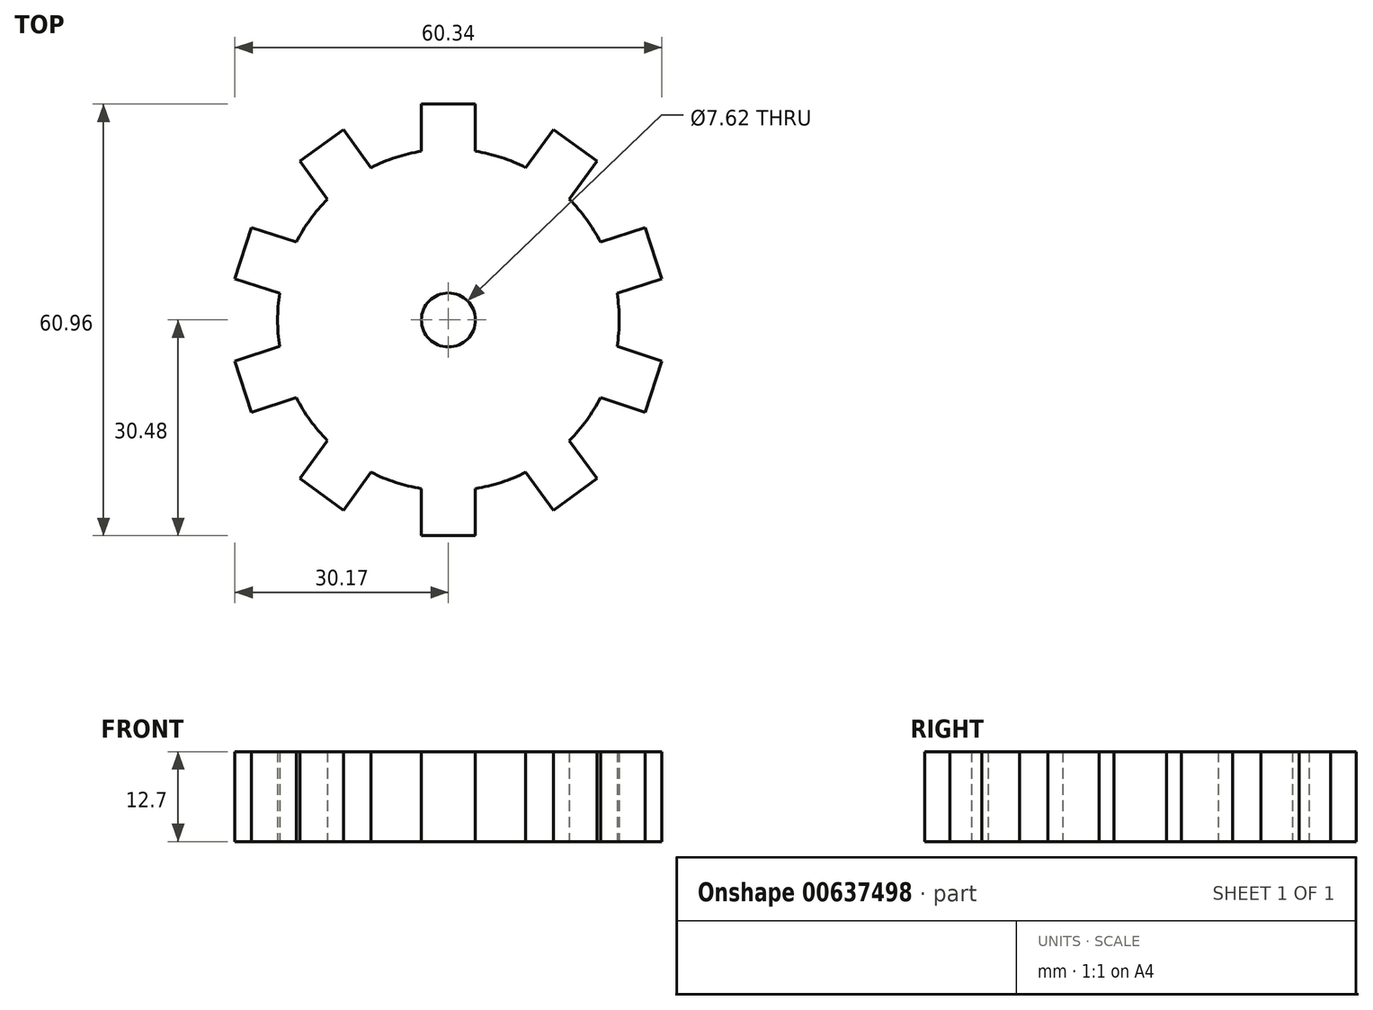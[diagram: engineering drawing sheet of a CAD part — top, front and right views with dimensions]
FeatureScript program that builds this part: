
annotation { "Feature Type Name" : "Feature", "Feature Type Description" : "" }
export const myFeature = defineFeature(function(context is Context, id is Id, definition is map)
    precondition{}
    {
        {
            var Q0;
            Q0=qCreatedBy(makeId("Top.planeOp"),FACE);
            var sketch = newSketch(context, id + "F0", { "sketchPlane" : qUnion([Q0])});
            skCircle(sketch, "E0", {"center": v(0, 0) * mm, "radius": 24.13 * mm});
            skLineSegment(sketch, "E1", {"start": v(0, 0) * mm, "end": v(-3.81, 0) * mm});
            skLineSegment(sketch, "E2", {"start": v(-3.81, 0) * mm, "end": v(-3.81, 30.48) * mm});
            skLineSegment(sketch, "E3", {"start": v(-3.81, 30.48) * mm, "end": v(3.8, 30.48) * mm});
            skLineSegment(sketch, "E4", {"start": v(3.81, 30.48) * mm, "end": v(3.81, 0) * mm});
            skLineSegment(sketch, "E5", {"start": v(3.81, 0) * mm, "end": v(0, 0) * mm});
            skLineSegment(sketch, "E6.1.0", {"start": v(-3.08, -2.24) * mm, "end": v(-21, 22.42) * mm});
            skLineSegment(sketch, "E6.1.1", {"start": v(-14.83, 26.9) * mm, "end": v(3.08, 2.24) * mm});
            skLineSegment(sketch, "E6.1.2", {"start": v(-21, 22.42) * mm, "end": v(-14.83, 26.9) * mm});
            skLineSegment(sketch, "E6.2.0", {"start": v(-1.18, -3.62) * mm, "end": v(-30.17, 5.8) * mm});
            skLineSegment(sketch, "E6.2.1", {"start": v(-27.81, 13.04) * mm, "end": v(1.18, 3.62) * mm});
            skLineSegment(sketch, "E6.2.2", {"start": v(-30.17, 5.8) * mm, "end": v(-27.81, 13.04) * mm});
            skLineSegment(sketch, "E6.3.0", {"start": v(1.18, -3.62) * mm, "end": v(-27.81, -13.04) * mm});
            skLineSegment(sketch, "E6.3.1", {"start": v(-30.17, -5.8) * mm, "end": v(-1.18, 3.62) * mm});
            skLineSegment(sketch, "E6.3.2", {"start": v(-27.81, -13.04) * mm, "end": v(-30.17, -5.8) * mm});
            skLineSegment(sketch, "E6.4.0", {"start": v(3.08, -2.24) * mm, "end": v(-14.83, -26.9) * mm});
            skLineSegment(sketch, "E6.4.1", {"start": v(-21, -22.42) * mm, "end": v(-3.08, 2.24) * mm});
            skLineSegment(sketch, "E6.4.2", {"start": v(-14.83, -26.9) * mm, "end": v(-21, -22.42) * mm});
            skLineSegment(sketch, "E6.5.0", {"start": v(3.81, 0) * mm, "end": v(3.81, -30.48) * mm});
            skLineSegment(sketch, "E6.5.1", {"start": v(-3.8, -30.48) * mm, "end": v(-3.8, 0) * mm});
            skLineSegment(sketch, "E6.5.2", {"start": v(3.81, -30.48) * mm, "end": v(-3.81, -30.48) * mm});
            skLineSegment(sketch, "E6.6.0", {"start": v(3.08, 2.24) * mm, "end": v(21, -22.42) * mm});
            skLineSegment(sketch, "E6.6.1", {"start": v(14.83, -26.9) * mm, "end": v(-3.08, -2.24) * mm});
            skLineSegment(sketch, "E6.6.2", {"start": v(21, -22.42) * mm, "end": v(14.83, -26.9) * mm});
            skLineSegment(sketch, "E6.7.0", {"start": v(1.18, 3.62) * mm, "end": v(30.17, -5.8) * mm});
            skLineSegment(sketch, "E6.7.1", {"start": v(27.81, -13.04) * mm, "end": v(-1.18, -3.62) * mm});
            skLineSegment(sketch, "E6.7.2", {"start": v(30.17, -5.8) * mm, "end": v(27.81, -13.04) * mm});
            skLineSegment(sketch, "E6.8.0", {"start": v(-1.18, 3.62) * mm, "end": v(27.81, 13.04) * mm});
            skLineSegment(sketch, "E6.8.1", {"start": v(30.17, 5.8) * mm, "end": v(1.18, -3.62) * mm});
            skLineSegment(sketch, "E6.8.2", {"start": v(27.81, 13.04) * mm, "end": v(30.17, 5.8) * mm});
            skLineSegment(sketch, "E6.9.0", {"start": v(-3.08, 2.24) * mm, "end": v(14.83, 26.9) * mm});
            skLineSegment(sketch, "E6.9.1", {"start": v(21, 22.42) * mm, "end": v(3.08, -2.24) * mm});
            skLineSegment(sketch, "E6.9.2", {"start": v(14.83, 26.9) * mm, "end": v(21, 22.42) * mm});
            skSolve(sketch);
        }
        {
            var Q0;
            Q0 = qSketchRegion(id + "F0", true);
            var Q1;
            {var subQ0=sQuery(id+"F0.wireOp",EDGE,"E6.12.1");var subQ1=sQuery(id+"F0.wireOp",EDGE,"E6.9.0");var subQ2=makeQuery(id+"F0.imprint","INTERSECT",VERTEX,{"derivedFrom":[subQ1,subQ0]});Q1=makeQuery(id+"F0.imprint","IMPRINT",FACE,{"disambiguationData":[TD([[makeQuery(id+"F0.imprint","IMPRINT",EDGE,{"disambiguationData":[TD([[subQ2,-1.0]])],"derivedFrom":subQ1}),1.0]])]});}
            var Q2;
            {var subQ0=sQuery(id+"F0.wireOp",EDGE,"E6.13.1");var subQ1=sQuery(id+"F0.wireOp",EDGE,"E6.10.0");var subQ2=makeQuery(id+"F0.imprint","INTERSECT",VERTEX,{"derivedFrom":[subQ1,subQ0]});Q2=makeQuery(id+"F0.imprint","IMPRINT",FACE,{"disambiguationData":[TD([[makeQuery(id+"F0.imprint","IMPRINT",EDGE,{"disambiguationData":[TD([[subQ2,-1.0]])],"derivedFrom":subQ1}),1.0]])]});}
            var Q3;
            {var subQ0=sQuery(id+"F0.wireOp",EDGE,"E6.13.1");var subQ1=sQuery(id+"F0.wireOp",EDGE,"E6.9.0");var subQ2=makeQuery(id+"F0.imprint","INTERSECT",VERTEX,{"derivedFrom":[subQ1,subQ0]});Q3=makeQuery(id+"F0.imprint","IMPRINT",FACE,{"disambiguationData":[TD([[makeQuery(id+"F0.imprint","IMPRINT",EDGE,{"disambiguationData":[TD([[subQ2,-1.0]])],"derivedFrom":subQ1}),1.0]])]});}
            var Q4;
            {var subQ0=sQuery(id+"F0.wireOp",EDGE,"E6.10.0");var subQ1=sQuery(id+"F0.wireOp",EDGE,"E4");var subQ2=makeQuery(id+"F0.imprint","INTERSECT",VERTEX,{"derivedFrom":[subQ1,subQ0]});Q4=makeQuery(id+"F0.imprint","IMPRINT",FACE,{"disambiguationData":[TD([[makeQuery(id+"F0.imprint","IMPRINT",EDGE,{"disambiguationData":[TD([[subQ2,-1.0]])],"derivedFrom":subQ1}),1.0]])]});}
            var Q5;
            {var subQ0=sQuery(id+"F0.wireOp",EDGE,"E6.11.0");var subQ1=sQuery(id+"F0.wireOp",EDGE,"E4");var subQ2=makeQuery(id+"F0.imprint","INTERSECT",VERTEX,{"derivedFrom":[subQ1,subQ0]});Q5=makeQuery(id+"F0.imprint","IMPRINT",FACE,{"disambiguationData":[TD([[makeQuery(id+"F0.imprint","IMPRINT",EDGE,{"disambiguationData":[TD([[subQ2,-1.0]])],"derivedFrom":subQ1}),1.0]])]});}
            var Q6;
            {var subQ0=sQuery(id+"F0.wireOp",EDGE,"E6.12.0");var subQ1=sQuery(id+"F0.wireOp",EDGE,"E4");var subQ2=makeQuery(id+"F0.imprint","INTERSECT",VERTEX,{"derivedFrom":[subQ1,subQ0]});Q6=makeQuery(id+"F0.imprint","IMPRINT",FACE,{"disambiguationData":[TD([[makeQuery(id+"F0.imprint","IMPRINT",EDGE,{"disambiguationData":[TD([[subQ2,-1.0]])],"derivedFrom":subQ1}),1.0]])]});}
            var Q7;
            {var subQ0=sQuery(id+"F0.wireOp",EDGE,"E6.12.0");var subQ1=sQuery(id+"F0.wireOp",EDGE,"E4");var subQ2=makeQuery(id+"F0.imprint","INTERSECT",VERTEX,{"derivedFrom":[subQ1,subQ0]});Q7=makeQuery(id+"F0.imprint","IMPRINT",FACE,{"disambiguationData":[TD([[makeQuery(id+"F0.imprint","IMPRINT",EDGE,{"disambiguationData":[TD([[subQ2,-1.0]])],"derivedFrom":subQ1}),-1.0]])]});}
            var Q8;
            {var subQ0=sQuery(id+"F0.wireOp",EDGE,"E6.11.0");var subQ1=sQuery(id+"F0.wireOp",EDGE,"E4");var subQ2=makeQuery(id+"F0.imprint","INTERSECT",VERTEX,{"derivedFrom":[subQ1,subQ0]});Q8=makeQuery(id+"F0.imprint","IMPRINT",FACE,{"disambiguationData":[TD([[makeQuery(id+"F0.imprint","IMPRINT",EDGE,{"disambiguationData":[TD([[subQ2,-1.0]])],"derivedFrom":subQ1}),-1.0]])]});}
            var Q9;
            {var subQ0=sQuery(id+"F0.wireOp",EDGE,"E6.13.0");var subQ1=sQuery(id+"F0.wireOp",EDGE,"E4");var subQ2=makeQuery(id+"F0.imprint","INTERSECT",VERTEX,{"derivedFrom":[subQ1,subQ0]});Q9=makeQuery(id+"F0.imprint","IMPRINT",FACE,{"disambiguationData":[TD([[makeQuery(id+"F0.imprint","IMPRINT",EDGE,{"disambiguationData":[TD([[subQ2,-1.0]])],"derivedFrom":subQ1}),-1.0]])]});}
            var Q10;
            {var subQ0=sQuery(id+"F0.wireOp",EDGE,"E6.13.0");var subQ1=sQuery(id+"F0.wireOp",EDGE,"E6.1.1");var subQ2=makeQuery(id+"F0.imprint","INTERSECT",VERTEX,{"derivedFrom":[subQ1,subQ0]});Q10=makeQuery(id+"F0.imprint","IMPRINT",FACE,{"disambiguationData":[TD([[makeQuery(id+"F0.imprint","IMPRINT",EDGE,{"disambiguationData":[TD([[subQ2,-1.0]])],"derivedFrom":subQ1}),-1.0]])]});}
            var Q11;
            {var subQ0=sQuery(id+"F0.wireOp",EDGE,"E6.12.0");var subQ1=sQuery(id+"F0.wireOp",EDGE,"E6.1.1");var subQ2=makeQuery(id+"F0.imprint","INTERSECT",VERTEX,{"derivedFrom":[subQ1,subQ0]});Q11=makeQuery(id+"F0.imprint","IMPRINT",FACE,{"disambiguationData":[TD([[makeQuery(id+"F0.imprint","IMPRINT",EDGE,{"disambiguationData":[TD([[subQ2,-1.0]])],"derivedFrom":subQ1}),-1.0]])]});}
            var Q12;
            {var subQ0=sQuery(id+"F0.wireOp",EDGE,"E6.11.0");var subQ1=sQuery(id+"F0.wireOp",EDGE,"E6.1.1");var subQ2=makeQuery(id+"F0.imprint","INTERSECT",VERTEX,{"derivedFrom":[subQ1,subQ0]});Q12=makeQuery(id+"F0.imprint","IMPRINT",FACE,{"disambiguationData":[TD([[makeQuery(id+"F0.imprint","IMPRINT",EDGE,{"disambiguationData":[TD([[subQ2,-1.0]])],"derivedFrom":subQ1}),-1.0]])]});}
            var Q13;
            {var subQ0=sQuery(id+"F0.wireOp",EDGE,"E6.12.0");var subQ1=sQuery(id+"F0.wireOp",EDGE,"E6.2.1");var subQ2=makeQuery(id+"F0.imprint","INTERSECT",VERTEX,{"derivedFrom":[subQ1,subQ0]});Q13=makeQuery(id+"F0.imprint","IMPRINT",FACE,{"disambiguationData":[TD([[makeQuery(id+"F0.imprint","IMPRINT",EDGE,{"disambiguationData":[TD([[subQ2,-1.0]])],"derivedFrom":subQ1}),-1.0]])]});}
            var Q14;
            {var subQ0=sQuery(id+"F0.wireOp",EDGE,"E6.10.0");var subQ1=sQuery(id+"F0.wireOp",EDGE,"E4");var subQ2=makeQuery(id+"F0.imprint","INTERSECT",VERTEX,{"derivedFrom":[subQ1,subQ0]});Q14=makeQuery(id+"F0.imprint","IMPRINT",FACE,{"disambiguationData":[TD([[makeQuery(id+"F0.imprint","IMPRINT",EDGE,{"disambiguationData":[TD([[subQ2,-1.0]])],"derivedFrom":subQ1}),-1.0]])]});}
            var Q15;
            {var subQ0=sQuery(id+"F0.wireOp",EDGE,"E6.9.0");var subQ1=sQuery(id+"F0.wireOp",EDGE,"E4");var subQ2=makeQuery(id+"F0.imprint","INTERSECT",VERTEX,{"derivedFrom":[subQ1,subQ0]});Q15=makeQuery(id+"F0.imprint","IMPRINT",FACE,{"disambiguationData":[TD([[makeQuery(id+"F0.imprint","IMPRINT",EDGE,{"disambiguationData":[TD([[subQ2,-1.0]])],"derivedFrom":subQ1}),1.0]])]});}
            var Q16;
            {var subQ0=sQuery(id+"F0.wireOp",EDGE,"E6.13.1");var subQ1=sQuery(id+"F0.wireOp",EDGE,"E6.7.0");var subQ2=makeQuery(id+"F0.imprint","INTERSECT",VERTEX,{"derivedFrom":[subQ1,subQ0]});Q16=makeQuery(id+"F0.imprint","IMPRINT",FACE,{"disambiguationData":[TD([[makeQuery(id+"F0.imprint","IMPRINT",EDGE,{"disambiguationData":[TD([[subQ2,-1.0]])],"derivedFrom":subQ1}),1.0]])]});}
            var Q17;
            {var subQ0=sQuery(id+"F0.wireOp",EDGE,"E6.12.1");var subQ1=sQuery(id+"F0.wireOp",EDGE,"E6.6.0");var subQ2=makeQuery(id+"F0.imprint","INTERSECT",VERTEX,{"derivedFrom":[subQ1,subQ0]});Q17=makeQuery(id+"F0.imprint","IMPRINT",FACE,{"disambiguationData":[TD([[makeQuery(id+"F0.imprint","IMPRINT",EDGE,{"disambiguationData":[TD([[subQ2,-1.0]])],"derivedFrom":subQ1}),1.0]])]});}
            var Q18;
            {var subQ0=sQuery(id+"F0.wireOp",EDGE,"E6.11.1");var subQ1=sQuery(id+"F0.wireOp",EDGE,"E6.5.0");var subQ2=makeQuery(id+"F0.imprint","INTERSECT",VERTEX,{"derivedFrom":[subQ1,subQ0]});Q18=makeQuery(id+"F0.imprint","IMPRINT",FACE,{"disambiguationData":[TD([[makeQuery(id+"F0.imprint","IMPRINT",EDGE,{"disambiguationData":[TD([[subQ2,-1.0]])],"derivedFrom":subQ1}),1.0]])]});}
            var Q19;
            {var subQ0=sQuery(id+"F0.wireOp",EDGE,"E6.10.1");var subQ1=sQuery(id+"F0.wireOp",EDGE,"E6.4.0");var subQ2=makeQuery(id+"F0.imprint","INTERSECT",VERTEX,{"derivedFrom":[subQ1,subQ0]});Q19=makeQuery(id+"F0.imprint","IMPRINT",FACE,{"disambiguationData":[TD([[makeQuery(id+"F0.imprint","IMPRINT",EDGE,{"disambiguationData":[TD([[subQ2,-1.0]])],"derivedFrom":subQ1}),1.0]])]});}
            var Q20;
            {var subQ0=sQuery(id+"F0.wireOp",EDGE,"E6.9.1");var subQ1=sQuery(id+"F0.wireOp",EDGE,"E6.3.0");var subQ2=makeQuery(id+"F0.imprint","INTERSECT",VERTEX,{"derivedFrom":[subQ1,subQ0]});Q20=makeQuery(id+"F0.imprint","IMPRINT",FACE,{"disambiguationData":[TD([[makeQuery(id+"F0.imprint","IMPRINT",EDGE,{"disambiguationData":[TD([[subQ2,-1.0]])],"derivedFrom":subQ1}),1.0]])]});}
            var Q21;
            {var subQ0=sQuery(id+"F0.wireOp",EDGE,"E6.8.1");var subQ1=sQuery(id+"F0.wireOp",EDGE,"E6.2.0");var subQ2=makeQuery(id+"F0.imprint","INTERSECT",VERTEX,{"derivedFrom":[subQ1,subQ0]});Q21=makeQuery(id+"F0.imprint","IMPRINT",FACE,{"disambiguationData":[TD([[makeQuery(id+"F0.imprint","IMPRINT",EDGE,{"disambiguationData":[TD([[subQ2,-1.0]])],"derivedFrom":subQ1}),1.0]])]});}
            var Q22;
            {var subQ0=sQuery(id+"F0.wireOp",EDGE,"E6.7.1");var subQ1=sQuery(id+"F0.wireOp",EDGE,"E6.1.0");var subQ2=makeQuery(id+"F0.imprint","INTERSECT",VERTEX,{"derivedFrom":[subQ1,subQ0]});Q22=makeQuery(id+"F0.imprint","IMPRINT",FACE,{"disambiguationData":[TD([[makeQuery(id+"F0.imprint","IMPRINT",EDGE,{"disambiguationData":[TD([[subQ2,-1.0]])],"derivedFrom":subQ1}),1.0]])]});}
            var Q23;
            {var subQ0=sQuery(id+"F0.wireOp",EDGE,"E6.6.1");var subQ1=sQuery(id+"F0.wireOp",EDGE,"E2");var subQ2=makeQuery(id+"F0.imprint","INTERSECT",VERTEX,{"derivedFrom":[subQ1,subQ0]});Q23=makeQuery(id+"F0.imprint","IMPRINT",FACE,{"disambiguationData":[TD([[makeQuery(id+"F0.imprint","IMPRINT",EDGE,{"disambiguationData":[TD([[subQ2,-1.0]])],"derivedFrom":subQ1}),1.0]])]});}
            var Q24;
            {var subQ0=sQuery(id+"F0.wireOp",EDGE,"E6.13.0");var subQ1=sQuery(id+"F0.wireOp",EDGE,"E6.3.1");var subQ2=makeQuery(id+"F0.imprint","INTERSECT",VERTEX,{"derivedFrom":[subQ1,subQ0]});Q24=makeQuery(id+"F0.imprint","IMPRINT",FACE,{"disambiguationData":[TD([[makeQuery(id+"F0.imprint","IMPRINT",EDGE,{"disambiguationData":[TD([[subQ2,-1.0]])],"derivedFrom":subQ1}),-1.0]])]});}
            var Q25;
            {var subQ0=sQuery(id+"F0.wireOp",EDGE,"E6.7.1");var subQ1=sQuery(id+"F0.wireOp",EDGE,"E6.3.0");var subQ2=makeQuery(id+"F0.imprint","INTERSECT",VERTEX,{"derivedFrom":[subQ1,subQ0]});Q25=makeQuery(id+"F0.imprint","IMPRINT",FACE,{"disambiguationData":[TD([[makeQuery(id+"F0.imprint","IMPRINT",EDGE,{"disambiguationData":[TD([[subQ2,-1.0]])],"derivedFrom":subQ1}),1.0]])]});}
            var Q26;
            {var subQ0=sQuery(id+"F0.wireOp",EDGE,"E6.6.1");var subQ1=sQuery(id+"F0.wireOp",EDGE,"E6.2.0");var subQ2=makeQuery(id+"F0.imprint","INTERSECT",VERTEX,{"derivedFrom":[subQ1,subQ0]});Q26=makeQuery(id+"F0.imprint","IMPRINT",FACE,{"disambiguationData":[TD([[makeQuery(id+"F0.imprint","IMPRINT",EDGE,{"disambiguationData":[TD([[subQ2,-1.0]])],"derivedFrom":subQ1}),1.0]])]});}
            var Q27;
            {var subQ0=sQuery(id+"F0.wireOp",EDGE,"E6.5.1");var subQ1=sQuery(id+"F0.wireOp",EDGE,"E6.1.0");var subQ2=makeQuery(id+"F0.imprint","INTERSECT",VERTEX,{"derivedFrom":[subQ1,subQ0]});Q27=makeQuery(id+"F0.imprint","IMPRINT",FACE,{"disambiguationData":[TD([[makeQuery(id+"F0.imprint","IMPRINT",EDGE,{"disambiguationData":[TD([[subQ2,-1.0]])],"derivedFrom":subQ1}),1.0]])]});}
            var Q28;
            {var subQ0=sQuery(id+"F0.wireOp",EDGE,"E6.4.1");var subQ1=sQuery(id+"F0.wireOp",EDGE,"E2");var subQ2=makeQuery(id+"F0.imprint","INTERSECT",VERTEX,{"derivedFrom":[subQ1,subQ0]});Q28=makeQuery(id+"F0.imprint","IMPRINT",FACE,{"disambiguationData":[TD([[makeQuery(id+"F0.imprint","IMPRINT",EDGE,{"disambiguationData":[TD([[subQ2,-1.0]])],"derivedFrom":subQ1}),1.0]])]});}
            var Q29;
            {var subQ0=sQuery(id+"F0.wireOp",EDGE,"E6.8.1");var subQ1=sQuery(id+"F0.wireOp",EDGE,"E6.4.0");var subQ2=makeQuery(id+"F0.imprint","INTERSECT",VERTEX,{"derivedFrom":[subQ1,subQ0]});Q29=makeQuery(id+"F0.imprint","IMPRINT",FACE,{"disambiguationData":[TD([[makeQuery(id+"F0.imprint","IMPRINT",EDGE,{"disambiguationData":[TD([[subQ2,-1.0]])],"derivedFrom":subQ1}),1.0]])]});}
            var Q30;
            {var subQ0=sQuery(id+"F0.wireOp",EDGE,"E6.9.1");var subQ1=sQuery(id+"F0.wireOp",EDGE,"E6.5.0");var subQ2=makeQuery(id+"F0.imprint","INTERSECT",VERTEX,{"derivedFrom":[subQ1,subQ0]});Q30=makeQuery(id+"F0.imprint","IMPRINT",FACE,{"disambiguationData":[TD([[makeQuery(id+"F0.imprint","IMPRINT",EDGE,{"disambiguationData":[TD([[subQ2,-1.0]])],"derivedFrom":subQ1}),1.0]])]});}
            var Q31;
            {var subQ0=sQuery(id+"F0.wireOp",EDGE,"E6.10.1");var subQ1=sQuery(id+"F0.wireOp",EDGE,"E6.6.0");var subQ2=makeQuery(id+"F0.imprint","INTERSECT",VERTEX,{"derivedFrom":[subQ1,subQ0]});Q31=makeQuery(id+"F0.imprint","IMPRINT",FACE,{"disambiguationData":[TD([[makeQuery(id+"F0.imprint","IMPRINT",EDGE,{"disambiguationData":[TD([[subQ2,-1.0]])],"derivedFrom":subQ1}),1.0]])]});}
            var Q32;
            {var subQ0=sQuery(id+"F0.wireOp",EDGE,"E6.11.1");var subQ1=sQuery(id+"F0.wireOp",EDGE,"E6.7.0");var subQ2=makeQuery(id+"F0.imprint","INTERSECT",VERTEX,{"derivedFrom":[subQ1,subQ0]});Q32=makeQuery(id+"F0.imprint","IMPRINT",FACE,{"disambiguationData":[TD([[makeQuery(id+"F0.imprint","IMPRINT",EDGE,{"disambiguationData":[TD([[subQ2,-1.0]])],"derivedFrom":subQ1}),1.0]])]});}
            var Q33;
            {var subQ0=sQuery(id+"F0.wireOp",EDGE,"E6.12.1");var subQ1=sQuery(id+"F0.wireOp",EDGE,"E6.8.0");var subQ2=makeQuery(id+"F0.imprint","INTERSECT",VERTEX,{"derivedFrom":[subQ1,subQ0]});Q33=makeQuery(id+"F0.imprint","IMPRINT",FACE,{"disambiguationData":[TD([[makeQuery(id+"F0.imprint","IMPRINT",EDGE,{"disambiguationData":[TD([[subQ2,-1.0]])],"derivedFrom":subQ1}),1.0]])]});}
            var Q34;
            {var subQ0=sQuery(id+"F0.wireOp",EDGE,"E6.12.1");var subQ1=sQuery(id+"F0.wireOp",EDGE,"E6.7.0");var subQ2=makeQuery(id+"F0.imprint","INTERSECT",VERTEX,{"derivedFrom":[subQ1,subQ0]});Q34=makeQuery(id+"F0.imprint","IMPRINT",FACE,{"disambiguationData":[TD([[makeQuery(id+"F0.imprint","IMPRINT",EDGE,{"disambiguationData":[TD([[subQ2,-1.0]])],"derivedFrom":subQ1}),1.0]])]});}
            var Q35;
            {var subQ0=sQuery(id+"F0.wireOp",EDGE,"E6.13.1");var subQ1=sQuery(id+"F0.wireOp",EDGE,"E6.8.0");var subQ2=makeQuery(id+"F0.imprint","INTERSECT",VERTEX,{"derivedFrom":[subQ1,subQ0]});Q35=makeQuery(id+"F0.imprint","IMPRINT",FACE,{"disambiguationData":[TD([[makeQuery(id+"F0.imprint","IMPRINT",EDGE,{"disambiguationData":[TD([[subQ2,-1.0]])],"derivedFrom":subQ1}),1.0]])]});}
            var Q36;
            {var subQ0=sQuery(id+"F0.wireOp",EDGE,"E6.11.1");var subQ1=sQuery(id+"F0.wireOp",EDGE,"E6.8.0");var subQ2=makeQuery(id+"F0.imprint","INTERSECT",VERTEX,{"derivedFrom":[subQ1,subQ0]});Q36=makeQuery(id+"F0.imprint","IMPRINT",FACE,{"disambiguationData":[TD([[makeQuery(id+"F0.imprint","IMPRINT",EDGE,{"disambiguationData":[TD([[subQ2,-1.0]])],"derivedFrom":subQ1}),1.0]])]});}
            var Q37;
            {var subQ0=sQuery(id+"F0.wireOp",EDGE,"E6.10.1");var subQ1=sQuery(id+"F0.wireOp",EDGE,"E6.7.0");var subQ2=makeQuery(id+"F0.imprint","INTERSECT",VERTEX,{"derivedFrom":[subQ1,subQ0]});Q37=makeQuery(id+"F0.imprint","IMPRINT",FACE,{"disambiguationData":[TD([[makeQuery(id+"F0.imprint","IMPRINT",EDGE,{"disambiguationData":[TD([[subQ2,-1.0]])],"derivedFrom":subQ1}),1.0]])]});}
            var Q38;
            {var subQ0=sQuery(id+"F0.wireOp",EDGE,"E6.11.1");var subQ1=sQuery(id+"F0.wireOp",EDGE,"E6.6.0");var subQ2=makeQuery(id+"F0.imprint","INTERSECT",VERTEX,{"derivedFrom":[subQ1,subQ0]});Q38=makeQuery(id+"F0.imprint","IMPRINT",FACE,{"disambiguationData":[TD([[makeQuery(id+"F0.imprint","IMPRINT",EDGE,{"disambiguationData":[TD([[subQ2,-1.0]])],"derivedFrom":subQ1}),1.0]])]});}
            var Q39;
            {var subQ0=sQuery(id+"F0.wireOp",EDGE,"E6.9.1");var subQ1=sQuery(id+"F0.wireOp",EDGE,"E6.6.0");var subQ2=makeQuery(id+"F0.imprint","INTERSECT",VERTEX,{"derivedFrom":[subQ1,subQ0]});Q39=makeQuery(id+"F0.imprint","IMPRINT",FACE,{"disambiguationData":[TD([[makeQuery(id+"F0.imprint","IMPRINT",EDGE,{"disambiguationData":[TD([[subQ2,-1.0]])],"derivedFrom":subQ1}),1.0]])]});}
            var Q40;
            {var subQ0=sQuery(id+"F0.wireOp",EDGE,"E6.10.1");var subQ1=sQuery(id+"F0.wireOp",EDGE,"E6.5.0");var subQ2=makeQuery(id+"F0.imprint","INTERSECT",VERTEX,{"derivedFrom":[subQ1,subQ0]});Q40=makeQuery(id+"F0.imprint","IMPRINT",FACE,{"disambiguationData":[TD([[makeQuery(id+"F0.imprint","IMPRINT",EDGE,{"disambiguationData":[TD([[subQ2,-1.0]])],"derivedFrom":subQ1}),1.0]])]});}
            var Q41;
            {var subQ0=sQuery(id+"F0.wireOp",EDGE,"E6.8.1");var subQ1=sQuery(id+"F0.wireOp",EDGE,"E6.5.0");var subQ2=makeQuery(id+"F0.imprint","INTERSECT",VERTEX,{"derivedFrom":[subQ1,subQ0]});Q41=makeQuery(id+"F0.imprint","IMPRINT",FACE,{"disambiguationData":[TD([[makeQuery(id+"F0.imprint","IMPRINT",EDGE,{"disambiguationData":[TD([[subQ2,-1.0]])],"derivedFrom":subQ1}),1.0]])]});}
            var Q42;
            {var subQ0=sQuery(id+"F0.wireOp",EDGE,"E6.9.1");var subQ1=sQuery(id+"F0.wireOp",EDGE,"E6.4.0");var subQ2=makeQuery(id+"F0.imprint","INTERSECT",VERTEX,{"derivedFrom":[subQ1,subQ0]});Q42=makeQuery(id+"F0.imprint","IMPRINT",FACE,{"disambiguationData":[TD([[makeQuery(id+"F0.imprint","IMPRINT",EDGE,{"disambiguationData":[TD([[subQ2,-1.0]])],"derivedFrom":subQ1}),1.0]])]});}
            var Q43;
            {var subQ0=sQuery(id+"F0.wireOp",EDGE,"E6.7.1");var subQ1=sQuery(id+"F0.wireOp",EDGE,"E6.4.0");var subQ2=makeQuery(id+"F0.imprint","INTERSECT",VERTEX,{"derivedFrom":[subQ1,subQ0]});Q43=makeQuery(id+"F0.imprint","IMPRINT",FACE,{"disambiguationData":[TD([[makeQuery(id+"F0.imprint","IMPRINT",EDGE,{"disambiguationData":[TD([[subQ2,-1.0]])],"derivedFrom":subQ1}),1.0]])]});}
            var Q44;
            {var subQ0=sQuery(id+"F0.wireOp",EDGE,"E6.8.1");var subQ1=sQuery(id+"F0.wireOp",EDGE,"E6.3.0");var subQ2=makeQuery(id+"F0.imprint","INTERSECT",VERTEX,{"derivedFrom":[subQ1,subQ0]});Q44=makeQuery(id+"F0.imprint","IMPRINT",FACE,{"disambiguationData":[TD([[makeQuery(id+"F0.imprint","IMPRINT",EDGE,{"disambiguationData":[TD([[subQ2,-1.0]])],"derivedFrom":subQ1}),1.0]])]});}
            var Q45;
            {var subQ0=sQuery(id+"F0.wireOp",EDGE,"E6.6.1");var subQ1=sQuery(id+"F0.wireOp",EDGE,"E6.3.0");var subQ2=makeQuery(id+"F0.imprint","INTERSECT",VERTEX,{"derivedFrom":[subQ1,subQ0]});Q45=makeQuery(id+"F0.imprint","IMPRINT",FACE,{"disambiguationData":[TD([[makeQuery(id+"F0.imprint","IMPRINT",EDGE,{"disambiguationData":[TD([[subQ2,-1.0]])],"derivedFrom":subQ1}),1.0]])]});}
            var Q46;
            {var subQ0=sQuery(id+"F0.wireOp",EDGE,"E6.7.1");var subQ1=sQuery(id+"F0.wireOp",EDGE,"E6.2.0");var subQ2=makeQuery(id+"F0.imprint","INTERSECT",VERTEX,{"derivedFrom":[subQ1,subQ0]});Q46=makeQuery(id+"F0.imprint","IMPRINT",FACE,{"disambiguationData":[TD([[makeQuery(id+"F0.imprint","IMPRINT",EDGE,{"disambiguationData":[TD([[subQ2,-1.0]])],"derivedFrom":subQ1}),1.0]])]});}
            var Q47;
            {var subQ0=sQuery(id+"F0.wireOp",EDGE,"E6.5.1");var subQ1=sQuery(id+"F0.wireOp",EDGE,"E6.2.0");var subQ2=makeQuery(id+"F0.imprint","INTERSECT",VERTEX,{"derivedFrom":[subQ1,subQ0]});Q47=makeQuery(id+"F0.imprint","IMPRINT",FACE,{"disambiguationData":[TD([[makeQuery(id+"F0.imprint","IMPRINT",EDGE,{"disambiguationData":[TD([[subQ2,-1.0]])],"derivedFrom":subQ1}),1.0]])]});}
            var Q48;
            {var subQ0=sQuery(id+"F0.wireOp",EDGE,"E6.6.1");var subQ1=sQuery(id+"F0.wireOp",EDGE,"E6.1.0");var subQ2=makeQuery(id+"F0.imprint","INTERSECT",VERTEX,{"derivedFrom":[subQ1,subQ0]});Q48=makeQuery(id+"F0.imprint","IMPRINT",FACE,{"disambiguationData":[TD([[makeQuery(id+"F0.imprint","IMPRINT",EDGE,{"disambiguationData":[TD([[subQ2,-1.0]])],"derivedFrom":subQ1}),1.0]])]});}
            var Q49;
            {var subQ0=sQuery(id+"F0.wireOp",EDGE,"E6.4.1");var subQ1=sQuery(id+"F0.wireOp",EDGE,"E6.1.0");var subQ2=makeQuery(id+"F0.imprint","INTERSECT",VERTEX,{"derivedFrom":[subQ1,subQ0]});Q49=makeQuery(id+"F0.imprint","IMPRINT",FACE,{"disambiguationData":[TD([[makeQuery(id+"F0.imprint","IMPRINT",EDGE,{"disambiguationData":[TD([[subQ2,-1.0]])],"derivedFrom":subQ1}),1.0]])]});}
            var Q50;
            {var subQ0=sQuery(id+"F0.wireOp",EDGE,"E6.5.1");var subQ1=sQuery(id+"F0.wireOp",EDGE,"E2");var subQ2=makeQuery(id+"F0.imprint","INTERSECT",VERTEX,{"derivedFrom":[subQ1,subQ0]});Q50=makeQuery(id+"F0.imprint","IMPRINT",FACE,{"disambiguationData":[TD([[makeQuery(id+"F0.imprint","IMPRINT",EDGE,{"disambiguationData":[TD([[subQ2,-1.0]])],"derivedFrom":subQ1}),1.0]])]});}
            var Q51;
            {var subQ0=sQuery(id+"F0.wireOp",EDGE,"E6.3.1");var subQ1=sQuery(id+"F0.wireOp",EDGE,"E2");var subQ2=makeQuery(id+"F0.imprint","INTERSECT",VERTEX,{"derivedFrom":[subQ1,subQ0]});Q51=makeQuery(id+"F0.imprint","IMPRINT",FACE,{"disambiguationData":[TD([[makeQuery(id+"F0.imprint","IMPRINT",EDGE,{"disambiguationData":[TD([[subQ2,-1.0]])],"derivedFrom":subQ1}),1.0]])]});}
            var Q52;
            {var subQ0=sQuery(id+"F0.wireOp",EDGE,"E6.4.1");var subQ1=sQuery(id+"F0.wireOp",EDGE,"E2");var subQ2=makeQuery(id+"F0.imprint","INTERSECT",VERTEX,{"derivedFrom":[subQ1,subQ0]});Q52=makeQuery(id+"F0.imprint","IMPRINT",FACE,{"disambiguationData":[TD([[makeQuery(id+"F0.imprint","IMPRINT",EDGE,{"disambiguationData":[TD([[subQ2,-1.0]])],"derivedFrom":subQ1}),-1.0]])]});}
            var Q53;
            {var subQ0=sQuery(id+"F0.wireOp",EDGE,"E6.2.1");var subQ1=sQuery(id+"F0.wireOp",EDGE,"E2");var subQ2=makeQuery(id+"F0.imprint","INTERSECT",VERTEX,{"derivedFrom":[subQ1,subQ0]});Q53=makeQuery(id+"F0.imprint","IMPRINT",FACE,{"disambiguationData":[TD([[makeQuery(id+"F0.imprint","IMPRINT",EDGE,{"disambiguationData":[TD([[subQ2,-1.0]])],"derivedFrom":subQ1}),-1.0]])]});}
            var Q54;
            {var subQ0=sQuery(id+"F0.wireOp",EDGE,"E6.3.1");var subQ1=sQuery(id+"F0.wireOp",EDGE,"E2");var subQ2=makeQuery(id+"F0.imprint","INTERSECT",VERTEX,{"derivedFrom":[subQ1,subQ0]});Q54=makeQuery(id+"F0.imprint","IMPRINT",FACE,{"disambiguationData":[TD([[makeQuery(id+"F0.imprint","IMPRINT",EDGE,{"disambiguationData":[TD([[subQ2,-1.0]])],"derivedFrom":subQ1}),-1.0]])]});}
            var Q55;
            {var subQ0=sQuery(id+"F0.wireOp",EDGE,"E6.13.0");var subQ1=sQuery(id+"F0.wireOp",EDGE,"E6.2.1");var subQ2=makeQuery(id+"F0.imprint","INTERSECT",VERTEX,{"derivedFrom":[subQ1,subQ0]});Q55=makeQuery(id+"F0.imprint","IMPRINT",FACE,{"disambiguationData":[TD([[makeQuery(id+"F0.imprint","IMPRINT",EDGE,{"disambiguationData":[TD([[subQ2,-1.0]])],"derivedFrom":subQ1}),-1.0]])]});}
            var Q56;
            {var subQ0=sQuery(id+"F0.wireOp",EDGE,"E6.13.1");var subQ1=sQuery(id+"F0.wireOp",EDGE,"E6.6.0");var subQ2=makeQuery(id+"F0.imprint","INTERSECT",VERTEX,{"derivedFrom":[subQ1,subQ0]});Q56=makeQuery(id+"F0.imprint","IMPRINT",FACE,{"disambiguationData":[TD([[makeQuery(id+"F0.imprint","IMPRINT",EDGE,{"disambiguationData":[TD([[subQ2,-1.0]])],"derivedFrom":subQ1}),1.0]])]});}
            var Q57;
            {var subQ1=sQuery(id+"F0.wireOp",EDGE,"E4");var subQ3=sQuery(id+"F0.wireOp",EDGE,"E6.8.0");var subQ4=makeQuery(id+"F0.imprint","INTERSECT",VERTEX,{"derivedFrom":[subQ1,subQ3]});Q57=makeQuery(id+"F0.imprint","IMPRINT",FACE,{"disambiguationData":[TD([[makeQuery(id+"F0.imprint","IMPRINT",EDGE,{"disambiguationData":[TD([[subQ4,-1.0]])],"derivedFrom":subQ3}),-1.0]])]});}
            var Q58;
            {var subQ0=sQuery(id+"F0.wireOp",EDGE,"E6.9.0");var subQ1=sQuery(id+"F0.wireOp",EDGE,"E4");var subQ2=makeQuery(id+"F0.imprint","INTERSECT",VERTEX,{"derivedFrom":[subQ1,subQ0]});Q58=makeQuery(id+"F0.imprint","IMPRINT",FACE,{"disambiguationData":[TD([[makeQuery(id+"F0.imprint","IMPRINT",EDGE,{"disambiguationData":[TD([[subQ2,-1.0]])],"derivedFrom":subQ1}),-1.0]])]});}
            var Q59;
            {var subQ0=sQuery(id+"F0.wireOp",EDGE,"E6.10.0");var subQ1=sQuery(id+"F0.wireOp",EDGE,"E6.1.1");var subQ2=makeQuery(id+"F0.imprint","INTERSECT",VERTEX,{"derivedFrom":[subQ1,subQ0]});Q59=makeQuery(id+"F0.imprint","IMPRINT",FACE,{"disambiguationData":[TD([[makeQuery(id+"F0.imprint","IMPRINT",EDGE,{"disambiguationData":[TD([[subQ2,-1.0]])],"derivedFrom":subQ1}),-1.0]])]});}
            var Q60;
            {var subQ0=sQuery(id+"F0.wireOp",EDGE,"E6.11.0");var subQ1=sQuery(id+"F0.wireOp",EDGE,"E6.2.1");var subQ2=makeQuery(id+"F0.imprint","INTERSECT",VERTEX,{"derivedFrom":[subQ1,subQ0]});Q60=makeQuery(id+"F0.imprint","IMPRINT",FACE,{"disambiguationData":[TD([[makeQuery(id+"F0.imprint","IMPRINT",EDGE,{"disambiguationData":[TD([[subQ2,-1.0]])],"derivedFrom":subQ1}),-1.0]])]});}
            var Q61;
            {var subQ0=sQuery(id+"F0.wireOp",EDGE,"E6.13.0");var subQ1=sQuery(id+"F0.wireOp",EDGE,"E6.4.1");var subQ2=makeQuery(id+"F0.imprint","INTERSECT",VERTEX,{"derivedFrom":[subQ1,subQ0]});Q61=makeQuery(id+"F0.imprint","IMPRINT",FACE,{"disambiguationData":[TD([[makeQuery(id+"F0.imprint","IMPRINT",EDGE,{"disambiguationData":[TD([[subQ2,-1.0]])],"derivedFrom":subQ1}),-1.0]])]});}
            var Q62;
            {var subQ0=sQuery(id+"F0.wireOp",EDGE,"E6.12.0");var subQ1=sQuery(id+"F0.wireOp",EDGE,"E6.3.1");var subQ2=makeQuery(id+"F0.imprint","INTERSECT",VERTEX,{"derivedFrom":[subQ1,subQ0]});Q62=makeQuery(id+"F0.imprint","IMPRINT",FACE,{"disambiguationData":[TD([[makeQuery(id+"F0.imprint","IMPRINT",EDGE,{"disambiguationData":[TD([[subQ2,-1.0]])],"derivedFrom":subQ1}),-1.0]])]});}
            var Q63;
            {var subQ0=sQuery(id+"F0.wireOp",EDGE,"E6.6.1");var subQ1=sQuery(id+"F0.wireOp",EDGE,"E2");var subQ2=makeQuery(id+"F0.imprint","INTERSECT",VERTEX,{"derivedFrom":[subQ1,subQ0]});Q63=makeQuery(id+"F0.imprint","IMPRINT",FACE,{"disambiguationData":[TD([[makeQuery(id+"F0.imprint","IMPRINT",EDGE,{"disambiguationData":[TD([[subQ2,-1.0]])],"derivedFrom":subQ1}),-1.0]])]});}
            var Q64;
            {var subQ0=sQuery(id+"F0.wireOp",EDGE,"E6.7.1");var subQ5=sQuery(id+"F0.wireOp",EDGE,"E6.1.0");var subQ6=makeQuery(id+"F0.imprint","INTERSECT",VERTEX,{"derivedFrom":[subQ5,subQ0]});Q64=makeQuery(id+"F0.imprint","IMPRINT",FACE,{"disambiguationData":[TD([[makeQuery(id+"F0.imprint","IMPRINT",EDGE,{"disambiguationData":[TD([[subQ6,-1.0]])],"derivedFrom":subQ5}),-1.0]])]});}
            var Q65;
            {var subQ0=sQuery(id+"F0.wireOp",EDGE,"E6.8.1");var subQ1=sQuery(id+"F0.wireOp",EDGE,"E6.1.0");var subQ2=makeQuery(id+"F0.imprint","INTERSECT",VERTEX,{"derivedFrom":[subQ1,subQ0]});Q65=makeQuery(id+"F0.imprint","IMPRINT",FACE,{"disambiguationData":[TD([[makeQuery(id+"F0.imprint","IMPRINT",EDGE,{"disambiguationData":[TD([[subQ2,-1.0]])],"derivedFrom":subQ1}),1.0]])]});}
            var Q66;
            {var subQ0=sQuery(id+"F0.wireOp",EDGE,"E6.9.1");var subQ1=sQuery(id+"F0.wireOp",EDGE,"E6.2.0");var subQ2=makeQuery(id+"F0.imprint","INTERSECT",VERTEX,{"derivedFrom":[subQ1,subQ0]});Q66=makeQuery(id+"F0.imprint","IMPRINT",FACE,{"disambiguationData":[TD([[makeQuery(id+"F0.imprint","IMPRINT",EDGE,{"disambiguationData":[TD([[subQ2,-1.0]])],"derivedFrom":subQ1}),1.0]])]});}
            var Q67;
            {var subQ0=sQuery(id+"F0.wireOp",EDGE,"E6.10.1");var subQ1=sQuery(id+"F0.wireOp",EDGE,"E6.3.0");var subQ2=makeQuery(id+"F0.imprint","INTERSECT",VERTEX,{"derivedFrom":[subQ1,subQ0]});Q67=makeQuery(id+"F0.imprint","IMPRINT",FACE,{"disambiguationData":[TD([[makeQuery(id+"F0.imprint","IMPRINT",EDGE,{"disambiguationData":[TD([[subQ2,-1.0]])],"derivedFrom":subQ1}),1.0]])]});}
            var Q68;
            {var subQ0=sQuery(id+"F0.wireOp",EDGE,"E6.11.1");var subQ1=sQuery(id+"F0.wireOp",EDGE,"E6.4.0");var subQ2=makeQuery(id+"F0.imprint","INTERSECT",VERTEX,{"derivedFrom":[subQ1,subQ0]});Q68=makeQuery(id+"F0.imprint","IMPRINT",FACE,{"disambiguationData":[TD([[makeQuery(id+"F0.imprint","IMPRINT",EDGE,{"disambiguationData":[TD([[subQ2,-1.0]])],"derivedFrom":subQ1}),1.0]])]});}
            var Q69;
            {var subQ0=sQuery(id+"F0.wireOp",EDGE,"E6.12.1");var subQ1=sQuery(id+"F0.wireOp",EDGE,"E6.5.0");var subQ2=makeQuery(id+"F0.imprint","INTERSECT",VERTEX,{"derivedFrom":[subQ1,subQ0]});Q69=makeQuery(id+"F0.imprint","IMPRINT",FACE,{"disambiguationData":[TD([[makeQuery(id+"F0.imprint","IMPRINT",EDGE,{"disambiguationData":[TD([[subQ2,-1.0]])],"derivedFrom":subQ1}),1.0]])]});}
            var Q70;
            {var subQ0=sQuery(id+"F0.wireOp",EDGE,"E6.9.0");var subQ1=sQuery(id+"F0.wireOp",EDGE,"E6.2.1");var subQ2=makeQuery(id+"F0.imprint","INTERSECT",VERTEX,{"derivedFrom":[subQ1,subQ0]});Q70=makeQuery(id+"F0.imprint","IMPRINT",FACE,{"disambiguationData":[TD([[makeQuery(id+"F0.imprint","IMPRINT",EDGE,{"disambiguationData":[TD([[subQ2,-1.0]])],"derivedFrom":subQ1}),-1.0]])]});}
            var Q71;
            {var subQ0=sQuery(id+"F0.wireOp",EDGE,"E6.9.0");var subQ1=sQuery(id+"F0.wireOp",EDGE,"E6.1.1");var subQ2=makeQuery(id+"F0.imprint","INTERSECT",VERTEX,{"derivedFrom":[subQ1,subQ0]});Q71=makeQuery(id+"F0.imprint","IMPRINT",FACE,{"disambiguationData":[TD([[makeQuery(id+"F0.imprint","IMPRINT",EDGE,{"disambiguationData":[TD([[subQ2,-1.0]])],"derivedFrom":subQ1}),-1.0]])]});}
            var Q72;
            {var subQ0=sQuery(id+"F0.wireOp",EDGE,"E6.8.0");var subQ1=sQuery(id+"F0.wireOp",EDGE,"E6.1.1");var subQ2=makeQuery(id+"F0.imprint","INTERSECT",VERTEX,{"derivedFrom":[subQ1,subQ0]});Q72=makeQuery(id+"F0.imprint","IMPRINT",FACE,{"disambiguationData":[TD([[makeQuery(id+"F0.imprint","IMPRINT",EDGE,{"disambiguationData":[TD([[subQ2,-1.0]])],"derivedFrom":subQ1}),-1.0]])]});}
            var Q73;
            {var subQ0=sQuery(id+"F0.wireOp",EDGE,"E6.7.0");var subQ1=sQuery(id+"F0.wireOp",EDGE,"E4");var subQ2=makeQuery(id+"F0.imprint","INTERSECT",VERTEX,{"derivedFrom":[subQ1,subQ0]});Q73=makeQuery(id+"F0.imprint","IMPRINT",FACE,{"disambiguationData":[TD([[makeQuery(id+"F0.imprint","IMPRINT",EDGE,{"disambiguationData":[TD([[subQ2,-1.0]])],"derivedFrom":subQ1}),-1.0]])]});}
            var Q74;
            {var subQ0=sQuery(id+"F0.wireOp",EDGE,"E6.7.0");var subQ1=sQuery(id+"F0.wireOp",EDGE,"E4");var subQ2=makeQuery(id+"F0.imprint","INTERSECT",VERTEX,{"derivedFrom":[subQ1,subQ0]});Q74=makeQuery(id+"F0.imprint","IMPRINT",FACE,{"disambiguationData":[TD([[makeQuery(id+"F0.imprint","IMPRINT",EDGE,{"disambiguationData":[TD([[subQ2,-1.0]])],"derivedFrom":subQ1}),1.0]])]});}
            var Q75;
            {var subQ1=sQuery(id+"F0.wireOp",EDGE,"E4");var subQ3=sQuery(id+"F0.wireOp",EDGE,"E6.6.0");var subQ4=makeQuery(id+"F0.imprint","INTERSECT",VERTEX,{"derivedFrom":[subQ1,subQ3]});Q75=makeQuery(id+"F0.imprint","IMPRINT",FACE,{"disambiguationData":[TD([[makeQuery(id+"F0.imprint","IMPRINT",EDGE,{"disambiguationData":[TD([[subQ4,-1.0]])],"derivedFrom":subQ3}),-1.0]])]});}
            var Q76;
            {var subQ0=sQuery(id+"F0.wireOp",EDGE,"E6.8.0");var subQ1=sQuery(id+"F0.wireOp",EDGE,"E4");var subQ2=makeQuery(id+"F0.imprint","INTERSECT",VERTEX,{"derivedFrom":[subQ1,subQ0]});Q76=makeQuery(id+"F0.imprint","IMPRINT",FACE,{"disambiguationData":[TD([[makeQuery(id+"F0.imprint","IMPRINT",EDGE,{"disambiguationData":[TD([[subQ2,-1.0]])],"derivedFrom":subQ1}),-1.0]])]});}
            var Q77;
            {var subQ6=sQuery(id+"F0.wireOp",EDGE,"E1");Q77=makeQuery(id+"F0.imprint","IMPRINT",FACE,{"disambiguationData":[TD([[makeQuery(id+"F0.imprint","IMPRINT",EDGE,{"derivedFrom":subQ6}),-1.0]])]});}
            var Q78;
            {var subQ6=sQuery(id+"F0.wireOp",EDGE,"E1");Q78=makeQuery(id+"F0.imprint","IMPRINT",FACE,{"disambiguationData":[TD([[makeQuery(id+"F0.imprint","IMPRINT",EDGE,{"derivedFrom":subQ6}),1.0]])]});}
            extrude(context, id + "F1", {"entities" : qUnion([Q0, Q1, Q2, Q3, Q4, Q5, Q6, Q7, Q8, Q9, Q10, Q11, Q12, Q13, Q14, Q15, Q16, Q17, Q18, Q19, Q20, Q21, Q22, Q23, Q24, Q25, Q26, Q27, Q28, Q29, Q30, Q31, Q32, Q33, Q34, Q35, Q36, Q37, Q38, Q39, Q40, Q41, Q42, Q43, Q44, Q45, Q46, Q47, Q48, Q49, Q50, Q51, Q52, Q53, Q54, Q55, Q56, Q57, Q58, Q59, Q60, Q61, Q62, Q63, Q64, Q65, Q66, Q67, Q68, Q69, Q70, Q71, Q72, Q73, Q74, Q75, Q76, Q77, Q78]), "depth" : 12.7 * mm, "offsetDistance" : 25.4 * mm});
        }
        {
            var Q0;
            Q0=makeQuery(id+"F1.opExtrude","CAP_FACE",FACE,{"disambiguationData":[OSD([sQuery(id+"F0.wireOp",EDGE,"E0"),sQuery(id+"F0.wireOp",EDGE,"E2"),sQuery(id+"F0.wireOp",EDGE,"E3"),sQuery(id+"F0.wireOp",EDGE,"E4"),sQuery(id+"F0.wireOp",EDGE,"E6.1.0"),sQuery(id+"F0.wireOp",EDGE,"E6.1.1"),sQuery(id+"F0.wireOp",EDGE,"E6.1.2"),sQuery(id+"F0.wireOp",EDGE,"E6.2.0"),sQuery(id+"F0.wireOp",EDGE,"E6.2.1"),sQuery(id+"F0.wireOp",EDGE,"E6.2.2"),sQuery(id+"F0.wireOp",EDGE,"E6.3.0"),sQuery(id+"F0.wireOp",EDGE,"E6.3.1"),sQuery(id+"F0.wireOp",EDGE,"E6.3.2"),sQuery(id+"F0.wireOp",EDGE,"E6.4.0"),sQuery(id+"F0.wireOp",EDGE,"E6.4.1"),sQuery(id+"F0.wireOp",EDGE,"E6.4.2"),sQuery(id+"F0.wireOp",EDGE,"E6.5.0"),sQuery(id+"F0.wireOp",EDGE,"E6.5.1"),sQuery(id+"F0.wireOp",EDGE,"E6.5.2"),sQuery(id+"F0.wireOp",EDGE,"E6.6.0"),sQuery(id+"F0.wireOp",EDGE,"E6.6.1"),sQuery(id+"F0.wireOp",EDGE,"E6.6.2"),sQuery(id+"F0.wireOp",EDGE,"E6.7.0"),sQuery(id+"F0.wireOp",EDGE,"E6.7.1"),sQuery(id+"F0.wireOp",EDGE,"E6.7.2"),sQuery(id+"F0.wireOp",EDGE,"E6.8.0"),sQuery(id+"F0.wireOp",EDGE,"E6.8.1"),sQuery(id+"F0.wireOp",EDGE,"E6.8.2"),sQuery(id+"F0.wireOp",EDGE,"E6.9.0"),sQuery(id+"F0.wireOp",EDGE,"E6.9.1"),sQuery(id+"F0.wireOp",EDGE,"E6.9.2")])],"isStart":false});
            var sketch = newSketch(context, id + "F2", { "sketchPlane" : qUnion([Q0])});
            skCircle(sketch, "E7", {"center": v(0, 0) * mm, "radius": 3.81 * mm});
            skSolve(sketch);
        }
        {
            var Q0;
            Q0=makeQuery(id+"F2.imprint","IMPRINT",FACE,{"disambiguationData":[TD([[makeQuery(id+"F2.imprint","IMPRINT",EDGE,{"derivedFrom":sQuery(id+"F2.wireOp",EDGE,"E7")}),1.0]])]});
            extrude(context, id + "F3", {"entities" : qUnion([Q0]), "operationType" : NewBodyOperationType.REMOVE, "oppositeDirection" : true, "depth" : 25.4 * mm, "offsetDistance" : 25.4 * mm});
        }
    });
